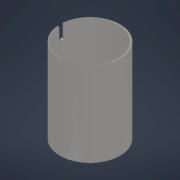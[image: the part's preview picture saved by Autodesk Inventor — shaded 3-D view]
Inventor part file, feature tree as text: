
AUTODESK INVENTOR PART (.ipt)
format: ipt  version: 2022 (Build 260153000, 153)  size: 119,296 bytes
history: native  units: mm
features: extrude x2, plane x1, sketch x1
ambient origin geometry x8: Origin, YZ Plane, XZ Plane, XY Plane, X Axis, Y Axis, Z Axis, Center Point
bodies: Solid1 (feature_tree)
feature tree (4):
  extrude  "Extrusion1"  Depth=8.0mm
  plane  "Work Plane1"
  extrude  "Extrusion2"  Depth=8.0mm TaperAngle=0.0deg
  sketch  "Sketch1"  dims[d0=88.9mm d1=2.9mm d2=124.0mm d3=0.0mm d7=50.0mm d8=0.0mm d16=8.0mm d17=15.0mm d18=15.0mm]
